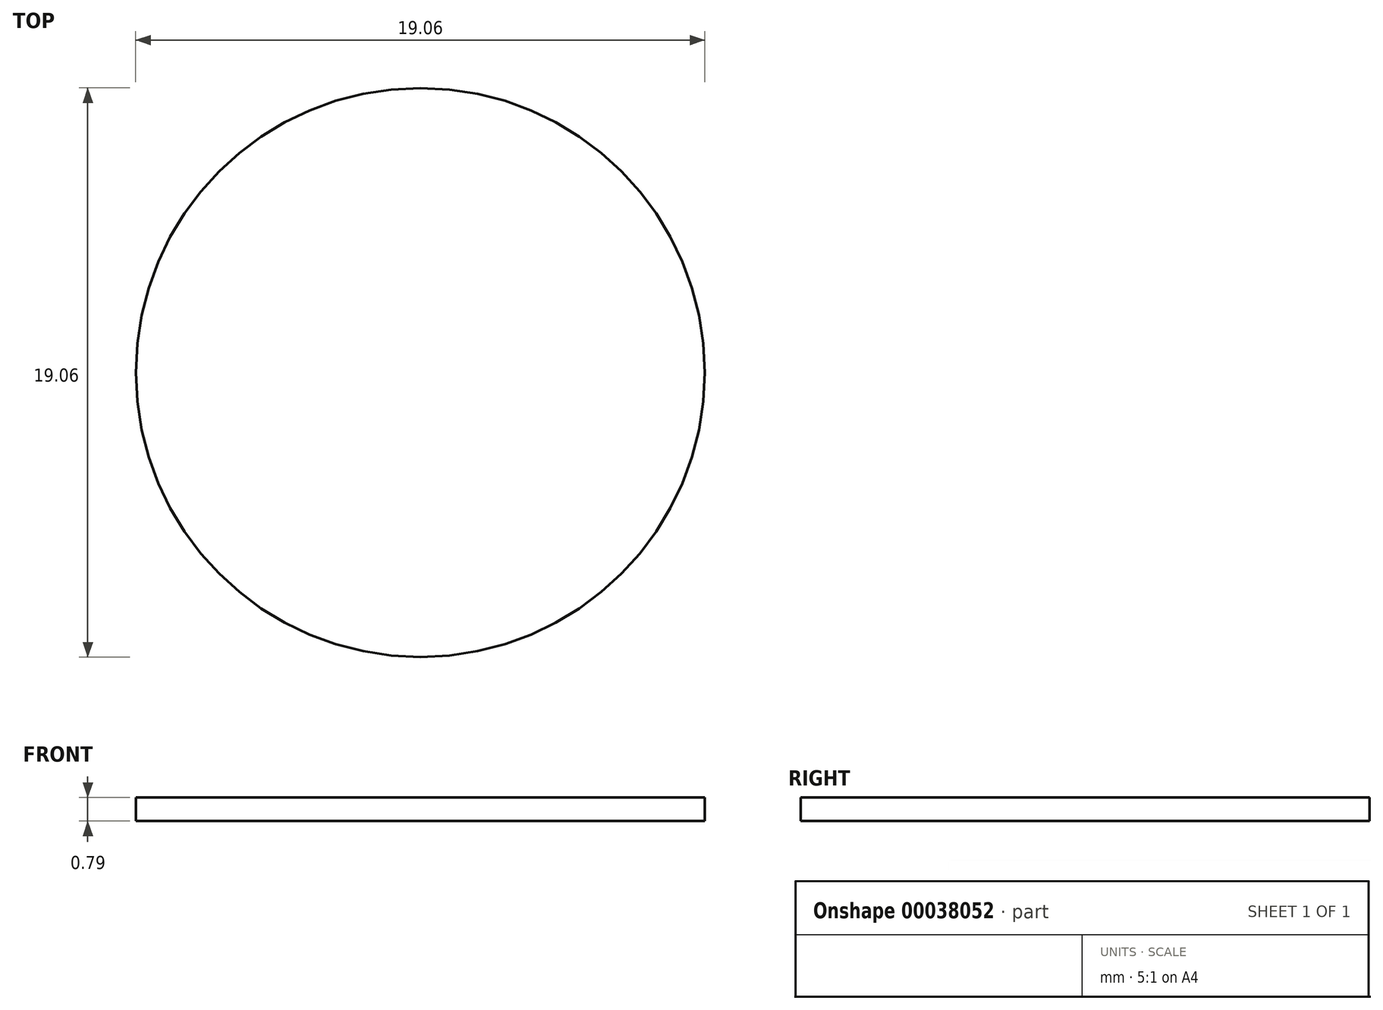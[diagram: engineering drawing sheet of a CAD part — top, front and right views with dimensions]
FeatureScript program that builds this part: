
annotation { "Feature Type Name" : "Feature", "Feature Type Description" : "" }
export const myFeature = defineFeature(function(context is Context, id is Id, definition is map)
    precondition{}
    {
        {
            var Q0;
            Q0=qCreatedBy(makeId("Top.planeOp"),FACE);
            var sketch = newSketch(context, id + "F0", { "sketchPlane" : qUnion([Q0])});
            skCircle(sketch, "E0", {"center": v(0, 0) * mm, "radius": 9.53 * mm});
            skSolve(sketch);
        }
        {
            var Q0;
            Q0 = qSketchRegion(id + "F0", true);
            extrude(context, id + "F1", {"entities" : qUnion([Q0]), "depth" : 0.8 * mm});
        }
    });
